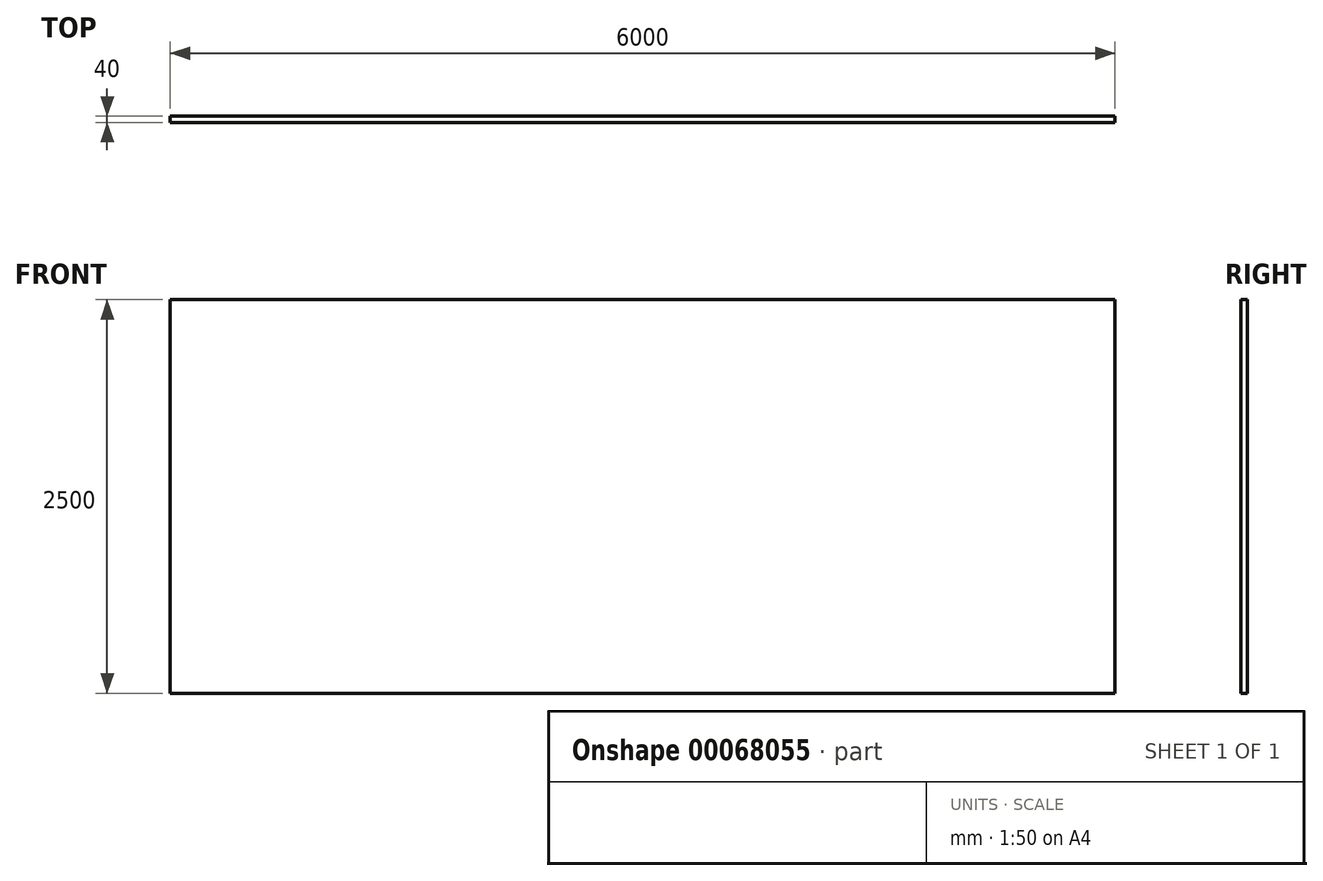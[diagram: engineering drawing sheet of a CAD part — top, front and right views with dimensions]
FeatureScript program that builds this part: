
annotation { "Feature Type Name" : "Feature", "Feature Type Description" : "" }
export const myFeature = defineFeature(function(context is Context, id is Id, definition is map)
    precondition{}
    {
        {
            var Q0;
            Q0=qCreatedBy(makeId("Front.planeOp"),FACE);
            var sketch = newSketch(context, id + "F0", { "sketchPlane" : qUnion([Q0])});
            skLineSegment(sketch, "E0.bottom", {"start": v(-76.71, 2439.66) * mm, "end": v(5923.29, 2439.66) * mm});
            skLineSegment(sketch, "E0.top", {"start": v(-76.71, -60.34) * mm, "end": v(5923.29, -60.34) * mm});
            skLineSegment(sketch, "E0.left", {"start": v(-76.71, 2439.66) * mm, "end": v(-76.71, -60.34) * mm});
            skLineSegment(sketch, "E0.right", {"start": v(5923.29, 2439.66) * mm, "end": v(5923.29, -60.34) * mm});
            skSolve(sketch);
        }
        {
            var Q0;
            Q0 = qSketchRegion(id + "F0", true);
            extrude(context, id + "F1", {"entities" : qUnion([Q0]), "depth" : 40 * mm});
        }
    });
